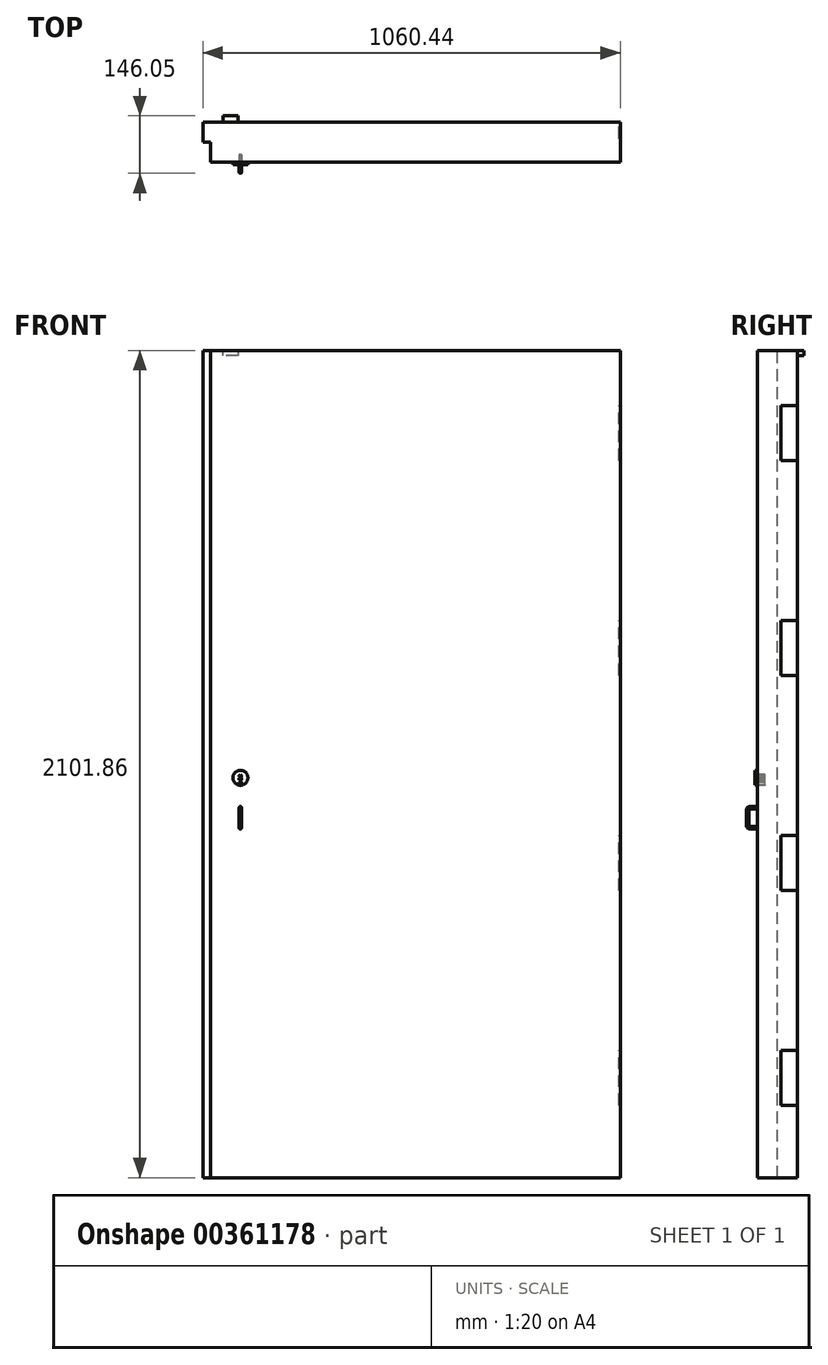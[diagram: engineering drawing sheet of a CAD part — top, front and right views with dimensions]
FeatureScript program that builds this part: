
annotation { "Feature Type Name" : "Feature", "Feature Type Description" : "" }
export const myFeature = defineFeature(function(context is Context, id is Id, definition is map)
    precondition{}
    {
        {
            var Q0;
            Q0=qCreatedBy(makeId("Front.planeOp"),FACE);
            var sketch = newSketch(context, id + "F0", { "sketchPlane" : qUnion([Q0])});
            skLineSegment(sketch, "E0.bottom", {"start": v(530.22, -1050.93) * mm, "end": v(-530.23, -1050.93) * mm});
            skLineSegment(sketch, "E0.top", {"start": v(530.23, 1050.93) * mm, "end": v(-530.23, 1050.93) * mm});
            skLineSegment(sketch, "E0.left", {"start": v(530.22, -1050.93) * mm, "end": v(530.23, 1050.93) * mm});
            skLineSegment(sketch, "E0.right", {"start": v(-530.23, -1050.93) * mm, "end": v(-530.23, 1050.93) * mm});
            skPoint(sketch, "E0.middle", {"position": v(0, 0) * mm});
            skSolve(sketch);
        }
        {
            var Q0;
            Q0=makeQuery(id+"F0.imprint","IMPRINT",FACE,{"disambiguationData":[TD([[makeQuery(id+"F0.imprint","IMPRINT",EDGE,{"derivedFrom":sQuery(id+"F0.wireOp",EDGE,"E0.bottom")}),-1.0]])]});
            extrude(context, id + "F1", {"entities" : qUnion([Q0]), "depth" : 101.6 * mm});
        }
        {
            var Q0;
            Q0=makeQuery(id+"F1.opExtrude","SWEPT_FACE",FACE,{"disambiguationData":[OSD([sQuery(id+"F0.wireOp",EDGE,"E0.top")])]});
            var sketch = newSketch(context, id + "F2", { "sketchPlane" : qUnion([Q0])});
            skLineSegment(sketch, "E1", {"start": v(-530.23, -101.6) * mm, "end": v(-511.18, -101.6) * mm});
            skLineSegment(sketch, "E2", {"start": v(-511.18, -101.6) * mm, "end": v(-511.18, -50.8) * mm});
            skLineSegment(sketch, "E3", {"start": v(-511.18, -50.8) * mm, "end": v(-530.23, -50.8) * mm});
            skLineSegment(sketch, "E4", {"start": v(-530.23, -50.8) * mm, "end": v(-530.23, -101.6) * mm});
            skSolve(sketch);
        }
        {
            var Q0;
            Q0=makeQuery(id+"F2.imprint","IMPRINT",FACE,{"disambiguationData":[TD([[makeQuery(id+"F2.imprint","IMPRINT",EDGE,{"derivedFrom":sQuery(id+"F2.wireOp",EDGE,"E1")}),-1.0]])]});
            extrude(context, id + "F3", {"entities" : qUnion([Q0]), "operationType" : NewBodyOperationType.REMOVE, "endBound" : BoundingType.UP_TO_NEXT, "oppositeDirection" : true, "depth" : 25.4 * mm});
        }
        {
            var Q0;
            Q0=makeQuery(id+"F1.opExtrude","SWEPT_FACE",FACE,{"disambiguationData":[OSD([sQuery(id+"F0.wireOp",EDGE,"E0.left")])]});
            var sketch = newSketch(context, id + "F4", { "sketchPlane" : qUnion([Q0])});
            skLineSegment(sketch, "E5", {"start": v(0, -866.78) * mm, "end": v(-41.9, -866.78) * mm});
            skLineSegment(sketch, "E6", {"start": v(-41.9, -866.78) * mm, "end": v(-41.9, -727.08) * mm});
            skLineSegment(sketch, "E7", {"start": v(-41.9, -727.08) * mm, "end": v(0, -727.08) * mm});
            skLineSegment(sketch, "E8", {"start": v(0, -727.08) * mm, "end": v(0, -866.78) * mm});
            skLineSegment(sketch, "E9.0.1.0", {"start": v(-41.9, -180.97) * mm, "end": v(0, -180.97) * mm});
            skLineSegment(sketch, "E9.0.1.1", {"start": v(-41.9, -320.68) * mm, "end": v(-41.9, -180.97) * mm});
            skLineSegment(sketch, "E9.0.1.2", {"start": v(0, -320.68) * mm, "end": v(-41.9, -320.68) * mm});
            skLineSegment(sketch, "E9.0.1.3", {"start": v(0, -180.97) * mm, "end": v(0, -320.68) * mm});
            skLineSegment(sketch, "E9.0.2.0", {"start": v(-41.9, 365.13) * mm, "end": v(0, 365.13) * mm});
            skLineSegment(sketch, "E9.0.2.1", {"start": v(-41.9, 225.42) * mm, "end": v(-41.9, 365.13) * mm});
            skLineSegment(sketch, "E9.0.2.2", {"start": v(0, 225.42) * mm, "end": v(-41.9, 225.42) * mm});
            skLineSegment(sketch, "E9.0.2.3", {"start": v(0, 365.13) * mm, "end": v(0, 225.42) * mm});
            skLineSegment(sketch, "E9.0.3.0", {"start": v(-41.9, 911.23) * mm, "end": v(0, 911.23) * mm});
            skLineSegment(sketch, "E9.0.3.1", {"start": v(-41.9, 771.52) * mm, "end": v(-41.9, 911.23) * mm});
            skLineSegment(sketch, "E9.0.3.2", {"start": v(0, 771.52) * mm, "end": v(-41.9, 771.52) * mm});
            skLineSegment(sketch, "E9.0.3.3", {"start": v(0, 911.23) * mm, "end": v(0, 771.52) * mm});
            skLineSegment(sketch, "E9.direction1", {"start": v(-41.9, -727.08) * mm, "end": v(-16.5, -727.08) * mm, "construction": true});
            skLineSegment(sketch, "E9.direction2", {"start": v(-41.9, -727.08) * mm, "end": v(-41.9, -180.97) * mm, "construction": true});
            skSolve(sketch);
        }
        {
            var Q0;
            Q0 = qSketchRegion(id + "F4", true);
            extrude(context, id + "F5", {"entities" : qUnion([Q0]), "operationType" : NewBodyOperationType.REMOVE, "oppositeDirection" : true, "depth" : 3.17 * mm});
        }
        {
            var Q0;
            Q0=makeQuery(id+"F1.opExtrude","CAP_FACE",FACE,{"disambiguationData":[OSD([sQuery(id+"F0.wireOp",EDGE,"E0.bottom"),sQuery(id+"F0.wireOp",EDGE,"E0.top"),sQuery(id+"F0.wireOp",EDGE,"E0.left"),sQuery(id+"F0.wireOp",EDGE,"E0.right")])],"isStart":false});
            var sketch = newSketch(context, id + "F6", { "sketchPlane" : qUnion([Q0])});
            skCircle(sketch, "E10", {"center": v(-434.98, -111.13) * mm, "radius": 3.18 * mm});
            skSolve(sketch);
        }
        {
            var Q0;
            Q0=sQuery(id+"F6.wireOp",VERTEX,"E10.center");
            var Q1;
            Q1=makeQuery(id+"F3.boolean.opBoolean","COPY",FACE,{"derivedFrom":makeQuery(id+"F3.opExtrude","SWEPT_FACE",FACE,{"disambiguationData":[OSD([sQuery(id+"F2.wireOp",EDGE,"E2")])]})});
            cPlane(context, id + "F7", {"entities" : qUnion([Q0, Q1]), "cplaneType" : CPlaneType.PLANE_POINT, "offset" : 25.4 * mm, "width" : 152.4 * mm, "height" : 152.4 * mm});
        }
        {
            var Q0;
            Q0=qCreatedBy(id+"F7.planeOp",FACE);
            var sketch = newSketch(context, id + "F8", { "sketchPlane" : qUnion([Q0])});
            skLineSegment(sketch, "E11", {"start": v(101.6, -111.13) * mm, "end": v(120.65, -111.13) * mm});
            skArc(sketch, "E12", {"start": v(127, -117.48) * mm, "mid": v(125.14, -112.98) * mm, "end": v(120.65, -111.13) * mm});
            skLineSegment(sketch, "E13", {"start": v(127, -117.48) * mm, "end": v(127, -155.58) * mm});
            skArc(sketch, "E14", {"start": v(120.65, -161.93) * mm, "mid": v(125.14, -160.07) * mm, "end": v(127, -155.58) * mm});
            skLineSegment(sketch, "E15", {"start": v(120.65, -161.93) * mm, "end": v(101.6, -161.93) * mm});
            skSolve(sketch);
        }
        {
            var Q0;
            Q0=makeQuery(id+"F6.imprint","IMPRINT",FACE,{"disambiguationData":[TD([[makeQuery(id+"F6.imprint","IMPRINT",EDGE,{"derivedFrom":sQuery(id+"F6.wireOp",EDGE,"E10")}),1.0]])]});
            var Q1;
            Q1=sQuery(id+"F8.wireOp",EDGE,"E11");
            var Q2;
            Q2=sQuery(id+"F8.wireOp",EDGE,"E12");
            var Q3;
            Q3=sQuery(id+"F8.wireOp",EDGE,"E13");
            var Q4;
            Q4=sQuery(id+"F8.wireOp",EDGE,"E14");
            var Q5;
            Q5=sQuery(id+"F8.wireOp",EDGE,"E15");
            sweep(context, id + "F9", {"operationType" : NewBodyOperationType.ADD, "profiles" : qUnion([Q0]), "path" : qUnion([Q1, Q2, Q3, Q4, Q5])});
        }
        {
            var Q0;
            Q0=makeQuery(id+"F1.opExtrude","CAP_FACE",FACE,{"disambiguationData":[OSD([sQuery(id+"F0.wireOp",EDGE,"E0.bottom"),sQuery(id+"F0.wireOp",EDGE,"E0.top"),sQuery(id+"F0.wireOp",EDGE,"E0.left"),sQuery(id+"F0.wireOp",EDGE,"E0.right")])],"isStart":true});
            var sketch = newSketch(context, id + "F10", { "sketchPlane" : qUnion([Q0])});
            skLineSegment(sketch, "E16", {"start": v(441.32, 1050.13) * mm, "end": v(441.32, 1037.43) * mm});
            skLineSegment(sketch, "E17", {"start": v(441.32, 1037.43) * mm, "end": v(479.43, 1037.43) * mm});
            skLineSegment(sketch, "E18", {"start": v(479.43, 1037.43) * mm, "end": v(479.43, 1050.13) * mm});
            skLineSegment(sketch, "E19", {"start": v(479.43, 1050.13) * mm, "end": v(441.32, 1050.13) * mm});
            skSolve(sketch);
        }
        {
            var Q0;
            Q0=makeQuery(id+"F10.imprint","IMPRINT",FACE,{"disambiguationData":[TD([[makeQuery(id+"F10.imprint","IMPRINT",EDGE,{"derivedFrom":sQuery(id+"F10.wireOp",EDGE,"E16")}),1.0]])]});
            extrude(context, id + "F11", {"entities" : qUnion([Q0]), "operationType" : NewBodyOperationType.ADD, "depth" : 15.87 * mm});
        }
        {
            var Q0;
            Q0=makeQuery(id+"F1.opExtrude","CAP_FACE",FACE,{"disambiguationData":[OSD([sQuery(id+"F0.wireOp",EDGE,"E0.bottom"),sQuery(id+"F0.wireOp",EDGE,"E0.top"),sQuery(id+"F0.wireOp",EDGE,"E0.left"),sQuery(id+"F0.wireOp",EDGE,"E0.right")])],"isStart":false});
            var sketch = newSketch(context, id + "F12", { "sketchPlane" : qUnion([Q0])});
            skCircle(sketch, "E20", {"center": v(-434.97, -34.92) * mm, "radius": 19.05 * mm});
            skSolve(sketch);
        }
        {
            var Q0;
            Q0=makeQuery(id+"F12.imprint","IMPRINT",FACE,{"disambiguationData":[TD([[makeQuery(id+"F12.imprint","IMPRINT",EDGE,{"derivedFrom":sQuery(id+"F12.wireOp",EDGE,"E20")}),1.0]])]});
            extrude(context, id + "F13", {"entities" : qUnion([Q0]), "operationType" : NewBodyOperationType.ADD, "depth" : 6.35 * mm});
        }
        {
            var Q0;
            Q0=makeQuery(id+"F13.opExtrude","CAP_FACE",FACE,{"disambiguationData":[OSD([sQuery(id+"F12.wireOp",EDGE,"E20")])],"isStart":false});
            var sketch = newSketch(context, id + "F14", { "sketchPlane" : qUnion([Q0])});
            skLineSegment(sketch, "E21", {"start": v(-438.5, -53.65) * mm, "end": v(-438.5, -47.46) * mm});
            skLineSegment(sketch, "E22", {"start": v(-438.5, -47.46) * mm, "end": v(-436.2, -47.46) * mm});
            skLineSegment(sketch, "E23", {"start": v(-436.2, -47.46) * mm, "end": v(-436.2, -44.91) * mm});
            skLineSegment(sketch, "E24", {"start": v(-436.2, -44.91) * mm, "end": v(-438.24, -42.77) * mm});
            skLineSegment(sketch, "E25", {"start": v(-438.24, -42.77) * mm, "end": v(-436, -41.96) * mm});
            skLineSegment(sketch, "E26", {"start": v(-436, -41.96) * mm, "end": v(-438.03, -40.22) * mm});
            skLineSegment(sketch, "E27", {"start": v(-438.03, -40.22) * mm, "end": v(-438.03, -35.63) * mm});
            skLineSegment(sketch, "E28", {"start": v(-438.03, -35.63) * mm, "end": v(-436.4, -33.6) * mm});
            skLineSegment(sketch, "E29", {"start": v(-436.4, -33.6) * mm, "end": v(-436.4, -31.25) * mm});
            skLineSegment(sketch, "E30", {"start": v(-436.4, -31.25) * mm, "end": v(-438.03, -31.25) * mm});
            skLineSegment(sketch, "E31", {"start": v(-438.03, -31.25) * mm, "end": v(-438.03, -28.6) * mm});
            skLineSegment(sketch, "E32", {"start": v(-438.03, -28.6) * mm, "end": v(-434.98, -26.05) * mm});
            skLineSegment(sketch, "E33.MirrorCS", {"start": v(-431.92, -28.6) * mm, "end": v(-434.98, -26.05) * mm});
            skLineSegment(sketch, "E34.MirrorCS", {"start": v(-431.92, -31.25) * mm, "end": v(-431.92, -28.6) * mm});
            skLineSegment(sketch, "E35.MirrorCS", {"start": v(-433.55, -31.25) * mm, "end": v(-431.92, -31.25) * mm});
            skLineSegment(sketch, "E36.MirrorCS", {"start": v(-433.55, -33.6) * mm, "end": v(-433.55, -31.25) * mm});
            skLineSegment(sketch, "E37.MirrorCS", {"start": v(-431.92, -35.63) * mm, "end": v(-433.55, -33.6) * mm});
            skLineSegment(sketch, "E38.MirrorCS", {"start": v(-431.92, -40.22) * mm, "end": v(-431.92, -35.63) * mm});
            skLineSegment(sketch, "E39.MirrorCS", {"start": v(-433.96, -41.96) * mm, "end": v(-431.92, -40.22) * mm});
            skLineSegment(sketch, "E40.MirrorCS", {"start": v(-431.71, -42.77) * mm, "end": v(-433.96, -41.96) * mm});
            skLineSegment(sketch, "E41.MirrorCS", {"start": v(-433.75, -44.91) * mm, "end": v(-431.71, -42.77) * mm});
            skLineSegment(sketch, "E42.MirrorCS", {"start": v(-433.75, -47.46) * mm, "end": v(-433.75, -44.91) * mm});
            skLineSegment(sketch, "E43.MirrorCS", {"start": v(-431.46, -47.46) * mm, "end": v(-433.75, -47.46) * mm});
            skLineSegment(sketch, "E44.MirrorCS", {"start": v(-431.46, -53.65) * mm, "end": v(-431.46, -47.46) * mm});
            skSolve(sketch);
        }
        {
            var Q0;
            {var subQ0=sQuery(id+"F14.wireOp",EDGE,"E21");Q0=makeQuery(id+"F14.imprint","IMPRINT",FACE,{"disambiguationData":[TD([[makeQuery(id+"F14.imprint","IMPRINT",EDGE,{"derivedFrom":subQ0}),-1.0]])]});}
            extrude(context, id + "F15", {"entities" : qUnion([Q0]), "operationType" : NewBodyOperationType.REMOVE, "oppositeDirection" : true, "depth" : 25.4 * mm});
        }
    });
